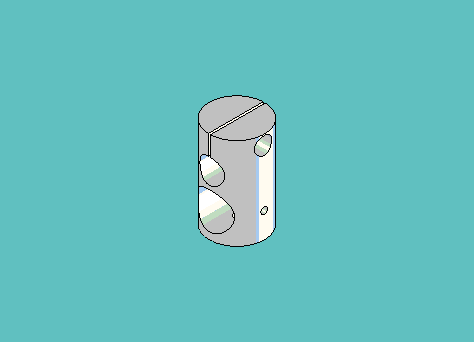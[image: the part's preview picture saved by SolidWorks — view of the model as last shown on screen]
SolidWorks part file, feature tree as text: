
SOLIDWORKS PART (.sldprt)
format: sldprt  version: not decoded by parser v0  size: 1,049,088 bytes
history: native  units: mm
features: sketch x9, boolean_combine x7, extrude x6, revolve x2, material x1, cut_extrude x1, plane x1 (+11 scaffold rows collapsed)
feature tree (38):
  scaffold x11  (default folders/planes/origin — collapsed)
  material  "Material <not specified>"
  sketch  "Sketch1"  dims[D1=31.75mm D2=9.525mm]
  revolve  "Revolve1"  Angle=360deg
  sketch  "Sketch2"  dims[c1.D1=2.7051mm c1.D2=2.2606mm c1.D3=8.7376mm c1.D4=28.3464mm c2.D3=8.7376mm c2.D4=28.3464mm]
  extrude  "Extrude1"  [1 undecoded]
  boolean_combine  "Combine1"
  sketch  "Sketch3"  dims[D1=2.2606mm]
  extrude  "Extrude2"  Depth=7.9756mm
  sketch  "Sketch5"  dims[c1.D4=~4.437453mm c1.D5=6.35mm c1.D1=8.7376mm c1.D2=6.35mm c1.D3=6.35mm c2.D4=9.525mm c2.D2=9.525mm c3.D4=9.525mm c3.D6=12.7mm c4.D4=3.175mm]
  revolve  "Revolve2"  Angle=360deg
  boolean_combine  "Combine4"
  sketch  "Sketch11"  dims[D1=~10.31875mm]
  cut_extrude  "Cut-Extrude1"  Depth=177.8mm
  boolean_combine  "Combine5"
  sketch  "Sketch6"  dims[D1=8.5852mm D2=20.6502mm]
  extrude  "Extrude3"  [1 undecoded]
  boolean_combine  "Combine6"
  sketch  "Sketch7"  dims[D1=0.381mm D2=0.381mm]
  extrude  "Extrude4"  [1 undecoded]
  boolean_combine  "Combine7"
  sketch  "Sketch9"  dims[c1.D1=~3.57124mm c1.D2=2.2606mm c1.D3=8.7376mm c1.D4=28.3464mm c2.D3=8.7376mm c2.D4=28.3464mm]
  extrude  "Extrude5"  [1 undecoded]
  boolean_combine  "Combine8"
  plane  "Plane1"  Offset=12.7mm
  sketch  "Sketch10"  dims[D1=~5.95376mm]
  extrude  "Extrude6"  Depth=7.9375mm
  boolean_combine  "Combine9"
decode coverage: 14 of 25 modeling features carry decoded parameters
note: ~ marks probable driven/reference dimensions
note: 4 parameter values undecoded
summary: no parameter record found for 4 features
note: suppression state not decoded; provenance and decode notes live in map.json
